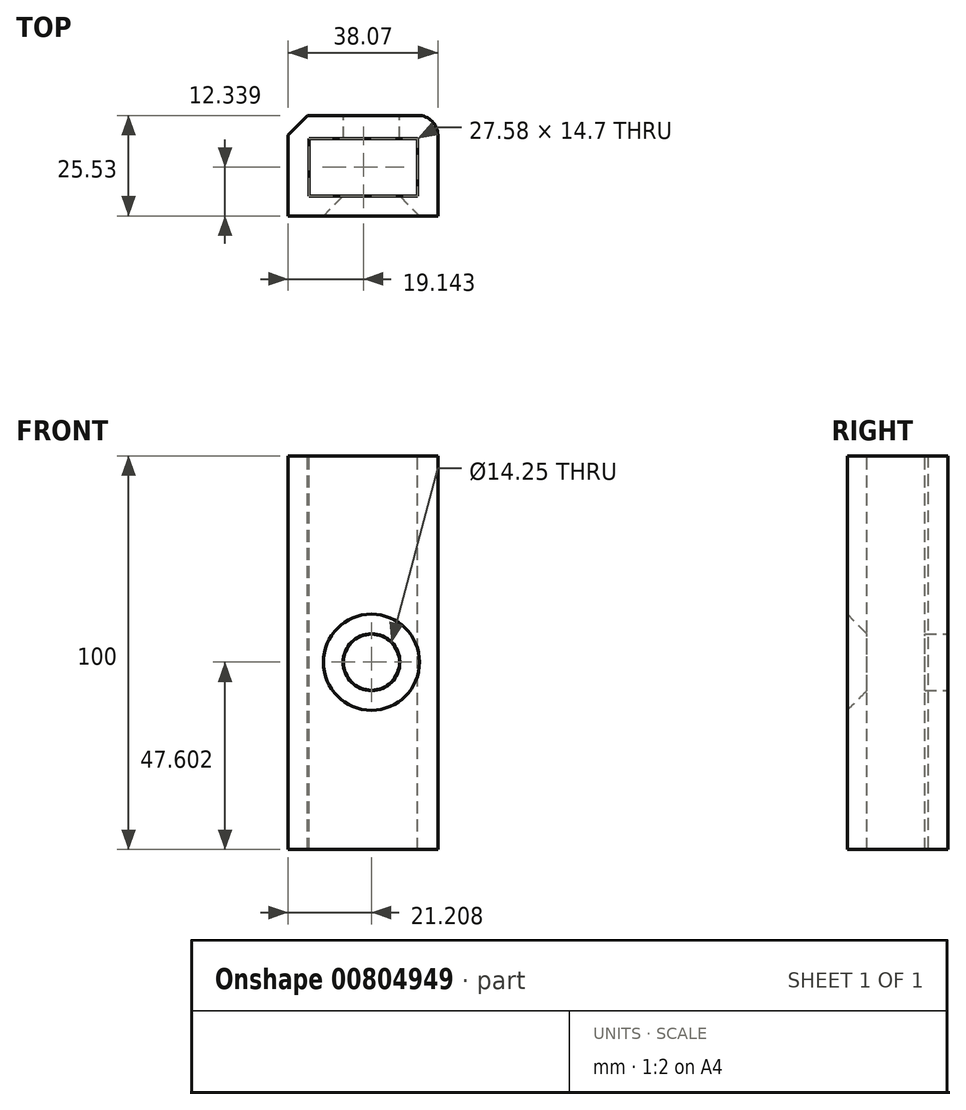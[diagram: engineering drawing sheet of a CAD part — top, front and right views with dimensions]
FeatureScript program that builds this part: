
annotation { "Feature Type Name" : "Feature", "Feature Type Description" : "" }
export const myFeature = defineFeature(function(context is Context, id is Id, definition is map)
    precondition{}
    {
        {
            var Q0;
            Q0=qCreatedBy(makeId("Top.planeOp"),FACE);
            var sketch = newSketch(context, id + "F0", { "sketchPlane" : qUnion([Q0])});
            skLineSegment(sketch, "E0.bottom", {"start": v(0, 0) * mm, "end": v(38.07, 0) * mm});
            skLineSegment(sketch, "E0.top", {"start": v(0, 25.53) * mm, "end": v(38.07, 25.53) * mm});
            skLineSegment(sketch, "E0.left", {"start": v(0, 0) * mm, "end": v(0, 25.53) * mm});
            skLineSegment(sketch, "E0.right", {"start": v(38.07, 0) * mm, "end": v(38.07, 25.53) * mm});
            skSolve(sketch);
        }
        {
            var Q0;
            Q0=makeQuery(id+"F0.imprint","IMPRINT",FACE,{"disambiguationData":[TD([[makeQuery(id+"F0.imprint","IMPRINT",EDGE,{"derivedFrom":sQuery(id+"F0.wireOp",EDGE,"E0.bottom")}),1.0]])]});
            extrude(context, id + "F1", {"entities" : qUnion([Q0]), "depth" : 100 * mm, "offsetDistance" : 25.4 * mm});
        }
        {
            var Q0;
            Q0=makeQuery(id+"F1.opExtrude","SWEPT_FACE",FACE,{"disambiguationData":[OSD([sQuery(id+"F0.wireOp",EDGE,"E0.right")])]});
            extrude(context, id + "F2", {"entities" : qUnion([Q0]), "operationType" : NewBodyOperationType.ADD, "oppositeDirection" : true, "depth" : 23.62 * mm, "offsetDistance" : 25.4 * mm});
        }
        {
            var Q0;
            Q0=makeQuery(id+"F1.opExtrude","SWEPT_FACE",FACE,{"disambiguationData":[OSD([sQuery(id+"F0.wireOp",EDGE,"E0.top")])]});
            var sketch = newSketch(context, id + "F3", { "sketchPlane" : qUnion([Q0])});
            skCircle(sketch, "E1", {"center": v(-21.2, 47.6) * mm, "radius": 7.12 * mm});
            skSolve(sketch);
        }
        {
            var Q0;
            Q0=makeQuery(id+"F3.imprint","IMPRINT",FACE,{"disambiguationData":[TD([[makeQuery(id+"F3.imprint","IMPRINT",EDGE,{"derivedFrom":sQuery(id+"F3.wireOp",EDGE,"E1")}),1.0]])]});
            extrude(context, id + "F4", {"entities" : qUnion([Q0]), "operationType" : NewBodyOperationType.REMOVE, "oppositeDirection" : true, "depth" : 56.64 * mm, "offsetDistance" : 25.4 * mm});
        }
        {
            var Q0;
            Q0=makeQuery(id+"F1.opExtrude","SWEPT_EDGE",EDGE,{"disambiguationData":[OSD([sQuery(id+"F0.wireOp",EDGE,"E0.top"),sQuery(id+"F0.wireOp",EDGE,"E0.right")])]});
            fillet(context, id + "F5", {"entities" : qUnion([Q0]), "radius" : 5.08 * mm, "tangentPropagation" : true, "allowEdgeOverflow" : false});
        }
        {
            var Q0;
            Q0=makeQuery(id+"F4.boolean.opBoolean","INTERSECT",EDGE,{"derivedFrom":[makeQuery(id+"F1.opExtrude","SWEPT_FACE",FACE,{"disambiguationData":[OSD([sQuery(id+"F0.wireOp",EDGE,"E0.bottom")])]}),makeQuery(id+"F4.opExtrude","SWEPT_FACE",FACE,{"disambiguationData":[OSD([sQuery(id+"F3.wireOp",EDGE,"E1")])]})]});
            chamfer(context, id + "F6", {"entities" : qUnion([Q0]), "width" : 5.08 * mm, "tangentPropagation" : true});
        }
        {
            var Q0;
            Q0=makeQuery(id+"F1.opExtrude","SWEPT_EDGE",EDGE,{"disambiguationData":[OSD([sQuery(id+"F0.wireOp",EDGE,"E0.top"),sQuery(id+"F0.wireOp",EDGE,"E0.left")])]});
            chamfer(context, id + "F7", {"entities" : qUnion([Q0]), "width" : 5 * mm, "tangentPropagation" : true});
        }
        {
            var Q0;
            Q0=makeQuery(id+"F1.opExtrude","CAP_FACE",FACE,{"disambiguationData":[OSD([sQuery(id+"F0.wireOp",EDGE,"E0.bottom"),sQuery(id+"F0.wireOp",EDGE,"E0.top"),sQuery(id+"F0.wireOp",EDGE,"E0.left"),sQuery(id+"F0.wireOp",EDGE,"E0.right")])],"isStart":false});
            var sketch = newSketch(context, id + "F8", { "sketchPlane" : qUnion([Q0])});
            skLineSegment(sketch, "E2.bottom", {"start": v(5.35, 19.69) * mm, "end": v(32.93, 19.69) * mm});
            skLineSegment(sketch, "E2.top", {"start": v(5.35, 4.99) * mm, "end": v(32.93, 4.99) * mm});
            skLineSegment(sketch, "E2.left", {"start": v(5.35, 19.69) * mm, "end": v(5.35, 4.99) * mm});
            skLineSegment(sketch, "E2.right", {"start": v(32.93, 19.69) * mm, "end": v(32.93, 4.99) * mm});
            skSolve(sketch);
        }
        {
            var Q0;
            Q0=makeQuery(id+"F8.imprint","IMPRINT",FACE,{"disambiguationData":[TD([[makeQuery(id+"F8.imprint","IMPRINT",EDGE,{"derivedFrom":sQuery(id+"F8.wireOp",EDGE,"E2.bottom")}),-1.0]])]});
            extrude(context, id + "F9", {"entities" : qUnion([Q0]), "operationType" : NewBodyOperationType.REMOVE, "oppositeDirection" : true, "depth" : 109.9 * mm, "offsetDistance" : 25 * mm});
        }
    });
